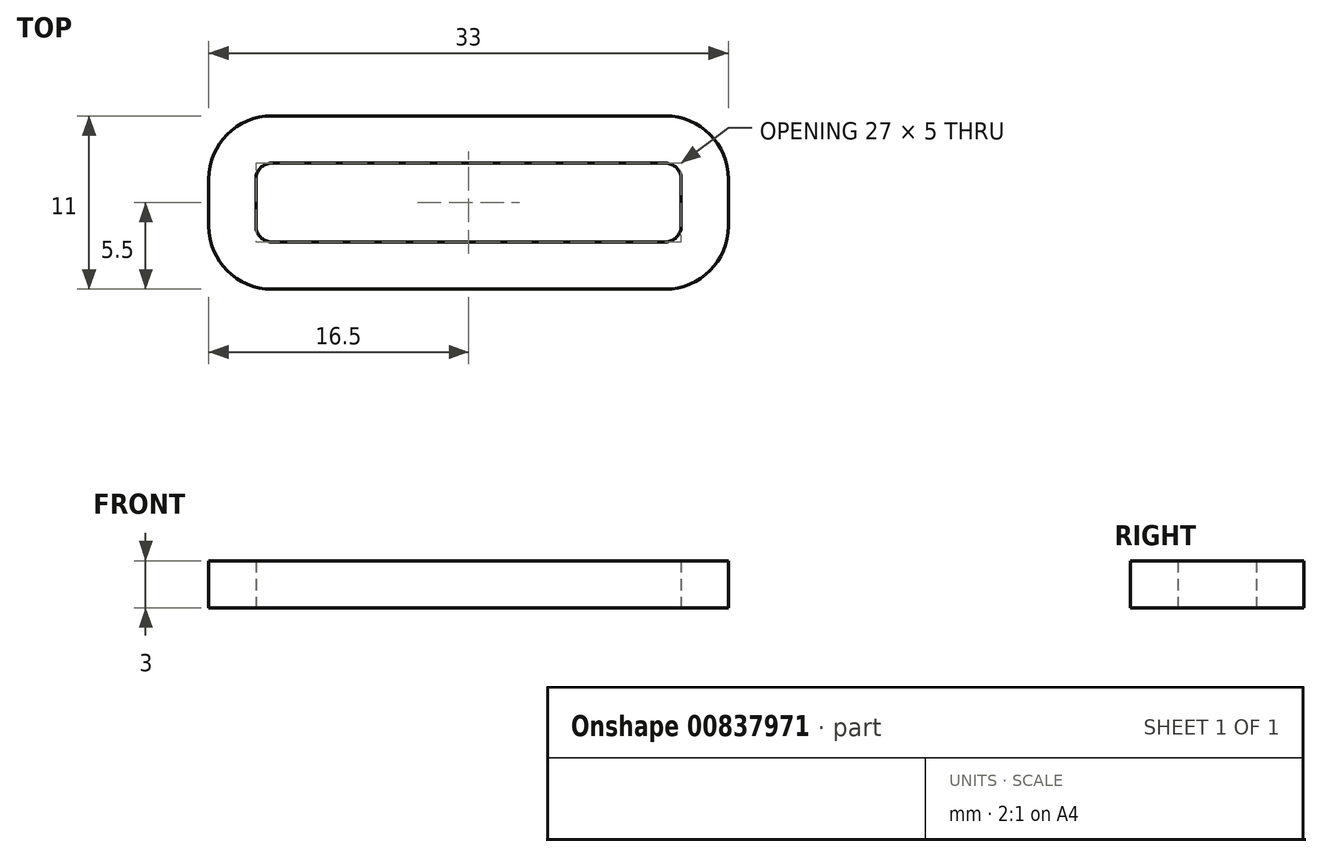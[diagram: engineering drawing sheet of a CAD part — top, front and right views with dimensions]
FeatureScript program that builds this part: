
annotation { "Feature Type Name" : "Feature", "Feature Type Description" : "" }
export const myFeature = defineFeature(function(context is Context, id is Id, definition is map)
    precondition{}
    {
        {
            var Q0;
            Q0=qCreatedBy(makeId("Top.planeOp"),FACE);
            var sketch = newSketch(context, id + "F0", { "sketchPlane" : qUnion([Q0])});
            skLineSegment(sketch, "E0.bottom", {"start": v(-12.5, 2.5) * mm, "end": v(12.5, 2.5) * mm});
            skLineSegment(sketch, "E0.top", {"start": v(-12.5, -2.5) * mm, "end": v(12.5, -2.5) * mm});
            skLineSegment(sketch, "E0.left", {"start": v(-13.5, 1.5) * mm, "end": v(-13.5, -1.5) * mm});
            skLineSegment(sketch, "E0.right", {"start": v(13.5, 1.5) * mm, "end": v(13.5, -1.5) * mm});
            skPoint(sketch, "E0.middle", {"position": v(0, 0) * mm});
            skPoint(sketch, "E1.visualSharp", {"position": v(-13.5, 2.5) * mm});
            skArc(sketch, "E1.filletArc", {"start": v(-12.5, 2.5) * mm, "mid": v(-13.2, 2.2) * mm, "end": v(-13.5, 1.5) * mm});
            skPoint(sketch, "E2.visualSharp", {"position": v(-13.5, -2.5) * mm});
            skArc(sketch, "E2.filletArc", {"start": v(-13.5, -1.5) * mm, "mid": v(-13.2, -2.2) * mm, "end": v(-12.5, -2.5) * mm});
            skPoint(sketch, "E3.visualSharp", {"position": v(13.5, 2.5) * mm});
            skArc(sketch, "E3.filletArc", {"start": v(13.5, 1.5) * mm, "mid": v(13.2, 2.2) * mm, "end": v(12.5, 2.5) * mm});
            skPoint(sketch, "E4.visualSharp", {"position": v(13.5, -2.5) * mm});
            skArc(sketch, "E4.filletArc", {"start": v(12.5, -2.5) * mm, "mid": v(13.2, -2.2) * mm, "end": v(13.5, -1.5) * mm});
            skArc(sketch, "E5.0", {"start": v(-12.5, 5.5) * mm, "mid": v(-15.33, 4.33) * mm, "end": v(-16.5, 1.5) * mm});
            skLineSegment(sketch, "E5.1", {"start": v(-16.5, 1.5) * mm, "end": v(-16.5, -1.5) * mm});
            skLineSegment(sketch, "E5.2", {"start": v(-12.5, 5.5) * mm, "end": v(12.5, 5.5) * mm});
            skArc(sketch, "E5.3", {"start": v(-16.5, -1.5) * mm, "mid": v(-15.33, -4.33) * mm, "end": v(-12.5, -5.5) * mm});
            skArc(sketch, "E5.4", {"start": v(16.5, 1.5) * mm, "mid": v(15.33, 4.33) * mm, "end": v(12.5, 5.5) * mm});
            skLineSegment(sketch, "E5.5", {"start": v(16.5, 1.5) * mm, "end": v(16.5, -1.5) * mm});
            skArc(sketch, "E5.6", {"start": v(12.5, -5.5) * mm, "mid": v(15.33, -4.33) * mm, "end": v(16.5, -1.5) * mm});
            skLineSegment(sketch, "E5.7", {"start": v(-12.5, -5.5) * mm, "end": v(12.5, -5.5) * mm});
            skSolve(sketch);
        }
        {
            var Q0;
            Q0 = qSketchRegion(id + "F0", true);
            extrude(context, id + "F1", {"entities" : qUnion([Q0]), "depth" : 3 * mm, "offsetDistance" : 25 * mm});
        }
    });
